# Revit family: BoelsRental_ArticulatingBoomLift_Genie_(Z34-22N)a
name_source: partatom
category: Site
units: mm (PartAtom-declared; Revit-internal decimal feet)

## family parameters
Always vertical = Yes
Cut with Voids When Loaded = No
OmniClass Number = 23.50.85.17
OmniClass Title = Telescoping Platforms
Part Type = Normal
Round Connector Dimension = Use Diameter
Shared = No
Work Plane-Based = No

## types (1)
- Z34-22N
    Assembly Code = E1030100
    AssetType = Movable
    BIMObjectName = BoelsRental_ArticulatingBoomLift_Genie_(Z34-22N)
    BoelsSubgroup = 18023 - Articulating telescopic boom lift 14.8m battery
    ClassificationName = Uniclass2015
    ClassificationValue = Pr_65_80_47_95
    Cost = 0 $
    Description = ARTICULATED BOOM LIFT, ELEC. < 13 M
    DocumentationCertificates = https://www.boels.com
    DocumentationInstallationGuide = https://www.boels.com
    DocumentationLiterature = https://www.boels.com
    DocumentationMaintenance = https://www.boels.com
    DocumentationTechnical = https://www.boels.com
    DurationUnit = Years
    ExpectedLife = 0
    IfcExportAs = IfcTransportElement
    IfcExportType = IfcTransportElementType
    Keynote = X
    Manufacturer = Boels Rental (Genie)
    ManufacturerName = Boels Rental (Genie)
    Material = Steel
    Model = Articulating Boom Lift - Z34-22N
    ModelNumber = Z34-22N
    ModelReference = Articulating Boom Lift
    NBSDescription = Vertical lifting platforms
    NBSObjectName = Boels Rental - Vertical lifting platforms
    NBSReference = 90-80-65/350
    NominalDepth = 1420 mm
    NominalHeight = 2000 mm  [stored 6.56168 ft]
    NominalLength = 5720 mm  [stored 18.7664 ft]
    ProductPageLink = https://www.boels.com
    ProductionYear = 2022
    Size = 1.47m x 2m x 5.72m
    Type Comments = Articulating Boom Lift - Z34-22N
    TypeName = Articulating Boom Lift - Z34-22N
    URL = https://www.boels.com
    WarrantyDurationLabor = 0
    WarrantyDurationParts = 0
    WarrantyDurationUnit = Years
    WarrantyGuarantorLabor = https://www.boels.com
    WarrantyGuarantorParts = https://www.boels.com
    _BSBibleVersion = 16
    _BimSpecGuid = 0
    _CurrentRevision = 1
    _DistributedBy = https://www.boels.com
    _ObjectUserGuide = https://www.boels.com

note: [stored X ft] marks values corroborated as IEEE doubles in the binary element streams (Revit-internal decimal feet)

## geometry (parser evidence)
native form markers: Sweep x54
no freeform markers — native parametric forms only
